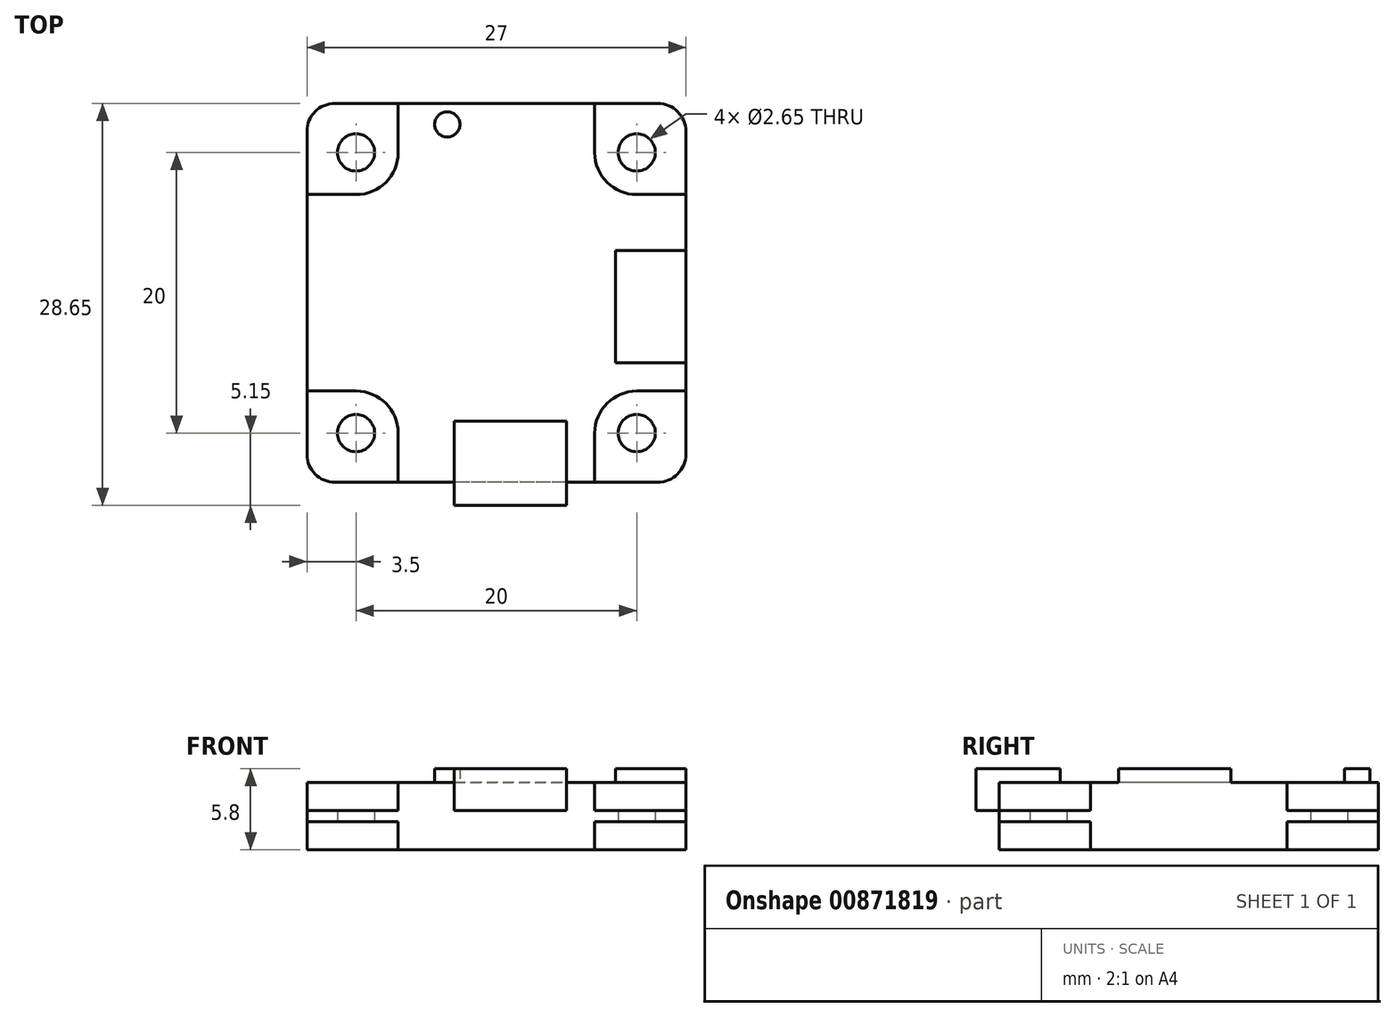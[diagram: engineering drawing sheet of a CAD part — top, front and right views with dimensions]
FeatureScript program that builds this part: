
annotation { "Feature Type Name" : "Feature", "Feature Type Description" : "" }
export const myFeature = defineFeature(function(context is Context, id is Id, definition is map)
    precondition{}
    {
        {
            var Q0;
            Q0=qCreatedBy(makeId("Top.planeOp"),FACE);
            var sketch = newSketch(context, id + "F0", { "sketchPlane" : qUnion([Q0])});
            skLineSegment(sketch, "E0.bottom", {"start": v(13.5, 13.5) * mm, "end": v(-13.5, 13.5) * mm});
            skLineSegment(sketch, "E0.top", {"start": v(13.5, -13.5) * mm, "end": v(-13.5, -13.5) * mm});
            skLineSegment(sketch, "E0.left", {"start": v(13.5, 13.5) * mm, "end": v(13.5, -13.5) * mm});
            skLineSegment(sketch, "E0.right", {"start": v(-13.5, 13.5) * mm, "end": v(-13.5, -13.5) * mm});
            skPoint(sketch, "E0.middle", {"position": v(0, 0) * mm});
            skLineSegment(sketch, "E1.bottom", {"start": v(10, 10) * mm, "end": v(-10, 10) * mm, "construction": true});
            skLineSegment(sketch, "E1.top", {"start": v(10, -10) * mm, "end": v(-10, -10) * mm, "construction": true});
            skLineSegment(sketch, "E1.left", {"start": v(10, 10) * mm, "end": v(10, -10) * mm, "construction": true});
            skLineSegment(sketch, "E1.right", {"start": v(-10, 10) * mm, "end": v(-10, -10) * mm, "construction": true});
            skSolve(sketch);
        }
        {
            var Q0;
            Q0=makeQuery(id+"F0.imprint","IMPRINT",FACE,{"disambiguationData":[TD([[makeQuery(id+"F0.imprint","IMPRINT",EDGE,{"derivedFrom":sQuery(id+"F0.wireOp",EDGE,"E0.bottom")}),1.0]])]});
            extrude(context, id + "F1", {"entities" : qUnion([Q0]), "depth" : 0.8 * mm, "offsetDistance" : 25 * mm});
        }
        {
            var Q0;
            Q0=sQuery(id+"F0.wireOp",VERTEX,"E1.bottom.end");
            var Q1;
            Q1=sQuery(id+"F0.wireOp",VERTEX,"E1.top.end");
            var Q2;
            Q2=sQuery(id+"F0.wireOp",VERTEX,"E1.bottom.start");
            var Q3;
            Q3=sQuery(id+"F0.wireOp",VERTEX,"E1.top.start");
            var Q4;
            Q4=makeQuery(id+"F1.opExtrude","SWEPT_BODY",BODY,{"disambiguationData":[OSD([sQuery(id+"F0.wireOp",EDGE,"E0.bottom"),sQuery(id+"F0.wireOp",EDGE,"E0.top"),sQuery(id+"F0.wireOp",EDGE,"E0.left"),sQuery(id+"F0.wireOp",EDGE,"E0.right")])]});
            hole(context, id + "F2", {"style" : HoleStyle.SIMPLE, "endStyle" : HoleEndStyle.THROUGH, "oppositeDirection" : true, "holeDiameter" : 2.65 * mm, "majorDiameter" : 5 * mm, "isTappedThrough" : true, "tappedDepth" : 12 * mm, "tapClearance" : 3, "locations" : qUnion([Q0, Q1, Q2, Q3]), "scope" : qUnion([Q4])});
        }
        {
            var Q0;
            Q0=makeQuery(id+"F1.opExtrude","SWEPT_EDGE",EDGE,{"disambiguationData":[OSD([sQuery(id+"F0.wireOp",EDGE,"E0.top"),sQuery(id+"F0.wireOp",EDGE,"E0.right")])]});
            var Q1;
            Q1=makeQuery(id+"F1.opExtrude","SWEPT_EDGE",EDGE,{"disambiguationData":[OSD([sQuery(id+"F0.wireOp",EDGE,"E0.bottom"),sQuery(id+"F0.wireOp",EDGE,"E0.right")])]});
            var Q2;
            Q2=makeQuery(id+"F1.opExtrude","SWEPT_EDGE",EDGE,{"disambiguationData":[OSD([sQuery(id+"F0.wireOp",EDGE,"E0.top"),sQuery(id+"F0.wireOp",EDGE,"E0.left")])]});
            var Q3;
            Q3=makeQuery(id+"F1.opExtrude","SWEPT_EDGE",EDGE,{"disambiguationData":[OSD([sQuery(id+"F0.wireOp",EDGE,"E0.bottom"),sQuery(id+"F0.wireOp",EDGE,"E0.left")])]});
            fillet(context, id + "F3", {"entities" : qUnion([Q0, Q1, Q2, Q3]), "radius" : 2 * mm, "tangentPropagation" : true, "allowEdgeOverflow" : false});
        }
        {
            var Q0;
            Q0=makeQuery(id+"F1.opExtrude","CAP_FACE",FACE,{"disambiguationData":[OSD([sQuery(id+"F0.wireOp",EDGE,"E0.bottom"),sQuery(id+"F0.wireOp",EDGE,"E0.top"),sQuery(id+"F0.wireOp",EDGE,"E0.left"),sQuery(id+"F0.wireOp",EDGE,"E0.right")])],"isStart":false});
            var sketch = newSketch(context, id + "F4", { "sketchPlane" : qUnion([Q0])});
            skLineSegment(sketch, "E2.bottom", {"start": v(8.5, 3) * mm, "end": v(13.5, 3) * mm});
            skLineSegment(sketch, "E2.top", {"start": v(8.5, -5) * mm, "end": v(13.5, -5) * mm});
            skLineSegment(sketch, "E2.left", {"start": v(8.5, 3) * mm, "end": v(8.5, -5) * mm});
            skLineSegment(sketch, "E2.right", {"start": v(13.5, 3) * mm, "end": v(13.5, -5) * mm});
            skLineSegment(sketch, "E3.bottom", {"start": v(-3, -9.15) * mm, "end": v(5, -9.15) * mm});
            skLineSegment(sketch, "E3.top", {"start": v(-3, -15.15) * mm, "end": v(5, -15.15) * mm});
            skLineSegment(sketch, "E3.left", {"start": v(-3, -9.15) * mm, "end": v(-3, -15.15) * mm});
            skLineSegment(sketch, "E3.right", {"start": v(5, -9.15) * mm, "end": v(5, -15.15) * mm});
            skCircle(sketch, "E4", {"center": v(-3.5, 12) * mm, "radius": 0.9 * mm});
            skSolve(sketch);
        }
        {
            var Q0;
            Q0 = qSketchRegion(id + "F4", true);
            extrude(context, id + "F5", {"entities" : qUnion([Q0]), "operationType" : NewBodyOperationType.ADD, "depth" : 3 * mm, "offsetDistance" : 25 * mm});
        }
        {
            var Q0;
            Q0=qCreatedBy(makeId("Top.planeOp"),FACE);
            var sketch = newSketch(context, id + "F6", { "sketchPlane" : qUnion([Q0])});
            skLineSegment(sketch, "E5.0.10", {"start": v(7, 13.5) * mm, "end": v(-7, 13.5) * mm});
            skLineSegment(sketch, "E5.0.12", {"start": v(-13.5, 7) * mm, "end": v(-13.5, -7) * mm});
            skCircle(sketch, "E6.0", {"center": v(-10, 10) * mm, "radius": 1.32 * mm, "construction": true});
            skLineSegment(sketch, "E7", {"start": v(-7, 10) * mm, "end": v(-7, 13.5) * mm});
            skLineSegment(sketch, "E8", {"start": v(-10, 7) * mm, "end": v(-13.5, 7) * mm});
            skArc(sketch, "E9", {"start": v(-7, 10) * mm, "mid": v(-7.88, 7.88) * mm, "end": v(-10, 7) * mm});
            skLineSegment(sketch, "E10.MirrorCS", {"start": v(10, 7) * mm, "end": v(13.5, 7) * mm});
            skArc(sketch, "E11.MirrorCS", {"start": v(7, 10) * mm, "mid": v(7.88, 7.88) * mm, "end": v(10, 7) * mm});
            skLineSegment(sketch, "E12.MirrorCS", {"start": v(7, 10) * mm, "end": v(7, 13.5) * mm});
            skLineSegment(sketch, "E13.MirrorCS", {"start": v(-10, -7) * mm, "end": v(-13.5, -7) * mm});
            skArc(sketch, "E14.MirrorCS", {"start": v(-7, -10) * mm, "mid": v(-7.88, -7.88) * mm, "end": v(-10, -7) * mm});
            skLineSegment(sketch, "E15.MirrorCS", {"start": v(-7, -10) * mm, "end": v(-7, -13.5) * mm});
            skLineSegment(sketch, "E16.MirrorCS", {"start": v(7, -10) * mm, "end": v(7, -13.5) * mm});
            skArc(sketch, "E17.MirrorCS", {"start": v(7, -10) * mm, "mid": v(7.88, -7.88) * mm, "end": v(10, -7) * mm});
            skLineSegment(sketch, "E18.MirrorCS", {"start": v(10, -7) * mm, "end": v(13.5, -7) * mm});
            skLineSegment(sketch, "E19.0", {"start": v(7, -13.5) * mm, "end": v(-7, -13.5) * mm});
            skLineSegment(sketch, "E20.0", {"start": v(13.5, 7) * mm, "end": v(13.5, -7) * mm});
            skSolve(sketch);
        }
        {
            var Q0;
            Q0 = qSketchRegion(id + "F6", true);
            extrude(context, id + "F7", {"entities" : qUnion([Q0]), "operationType" : NewBodyOperationType.ADD, "depth" : 2.8 * mm, "offsetDistance" : 25 * mm, "hasSecondDirection" : true, "secondDirectionOppositeDirection" : true, "secondDirectionDepth" : 2 * mm});
        }
    });
